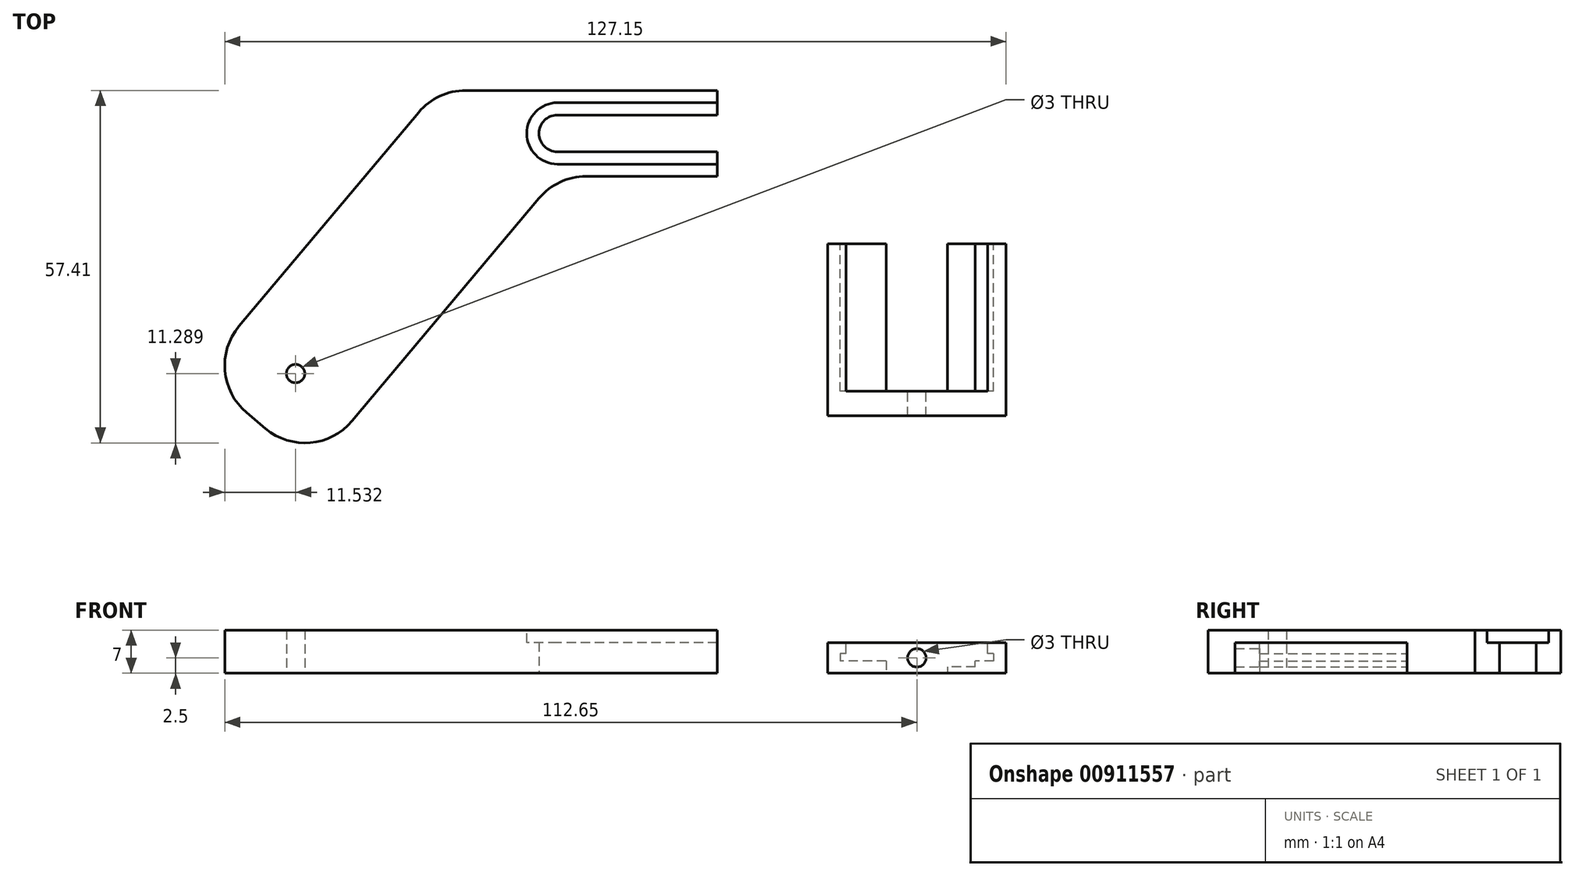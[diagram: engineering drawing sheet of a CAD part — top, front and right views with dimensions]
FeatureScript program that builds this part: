
annotation { "Feature Type Name" : "Feature", "Feature Type Description" : "" }
export const myFeature = defineFeature(function(context is Context, id is Id, definition is map)
    precondition{}
    {
        {
            var Q0;
            Q0=qCreatedBy(makeId("Top.planeOp"),FACE);
            var sketch = newSketch(context, id + "F0", { "sketchPlane" : qUnion([Q0])});
            skLineSegment(sketch, "E0.bottom", {"start": v(0, 7) * mm, "end": v(-40.92, 7) * mm});
            skLineSegment(sketch, "E0.top", {"start": v(0, -7) * mm, "end": v(-21.34, -7) * mm});
            skLineSegment(sketch, "E0.left", {"start": v(0, 7) * mm, "end": v(0, 3) * mm});
            skLineSegment(sketch, "E1.bottom", {"start": v(0, 3) * mm, "end": v(-26, 3) * mm});
            skLineSegment(sketch, "E1.top", {"start": v(0, -3) * mm, "end": v(-26, -3) * mm});
            skArc(sketch, "E2", {"start": v(-26, 3) * mm, "mid": v(-29, 0) * mm, "end": v(-26, -3) * mm});
            skLineSegment(sketch, "E3.trimOffspring", {"start": v(0, -3) * mm, "end": v(0, -7) * mm});
            skLineSegment(sketch, "E4", {"start": v(-29, -10.57) * mm, "end": v(-59.42, -46.83) * mm});
            skLineSegment(sketch, "E5", {"start": v(-73.51, -48.07) * mm, "end": v(-76.58, -45.5) * mm});
            skLineSegment(sketch, "E6", {"start": v(-77.81, -31.4) * mm, "end": v(-48.58, 3.43) * mm});
            skPoint(sketch, "E7.visualSharp", {"position": v(-84.24, -39.07) * mm});
            skArc(sketch, "E7.filletArc", {"start": v(-77.81, -31.4) * mm, "mid": v(-80.11, -38.7) * mm, "end": v(-76.58, -45.5) * mm});
            skPoint(sketch, "E8.visualSharp", {"position": v(-65.85, -54.5) * mm});
            skArc(sketch, "E8.filletArc", {"start": v(-73.51, -48.07) * mm, "mid": v(-66.21, -50.37) * mm, "end": v(-59.42, -46.83) * mm});
            skPoint(sketch, "E9.visualSharp", {"position": v(-45.58, 7) * mm});
            skArc(sketch, "E9.filletArc", {"start": v(-40.92, 7) * mm, "mid": v(-45.15, 6.06) * mm, "end": v(-48.58, 3.43) * mm});
            skPoint(sketch, "E10.visualSharp", {"position": v(-26, -7) * mm});
            skArc(sketch, "E10.filletArc", {"start": v(-21.34, -7) * mm, "mid": v(-25.56, -7.94) * mm, "end": v(-29, -10.57) * mm});
            skCircle(sketch, "E11", {"center": v(-68.62, -39.12) * mm, "radius": 1.5 * mm});
            skPoint(sketch, "E12.start.orphan", {"position": v(-75.05, -46.78) * mm});
            skSolve(sketch);
        }
        {
            var Q0;
            Q0=makeQuery(id+"F0.imprint","IMPRINT",FACE,{"disambiguationData":[TD([[makeQuery(id+"F0.imprint","IMPRINT",EDGE,{"derivedFrom":sQuery(id+"F0.wireOp",EDGE,"E0.bottom")}),1.0]])]});
            extrude(context, id + "F1", {"entities" : qUnion([Q0]), "depth" : 7 * mm, "offsetDistance" : 25 * mm});
        }
        {
            var Q0;
            Q0=makeQuery(id+"F1.opExtrude","CAP_FACE",FACE,{"disambiguationData":[OSD([sQuery(id+"F0.wireOp",EDGE,"E0.bottom"),sQuery(id+"F0.wireOp",EDGE,"E0.top"),sQuery(id+"F0.wireOp",EDGE,"E0.left"),sQuery(id+"F0.wireOp",EDGE,"E1.bottom"),sQuery(id+"F0.wireOp",EDGE,"E1.top"),sQuery(id+"F0.wireOp",EDGE,"E2"),sQuery(id+"F0.wireOp",EDGE,"E3.trimOffspring"),sQuery(id+"F0.wireOp",EDGE,"E4"),sQuery(id+"F0.wireOp",EDGE,"E5"),sQuery(id+"F0.wireOp",EDGE,"E6"),sQuery(id+"F0.wireOp",EDGE,"E7.filletArc"),sQuery(id+"F0.wireOp",EDGE,"E8.filletArc"),sQuery(id+"F0.wireOp",EDGE,"E9.filletArc"),sQuery(id+"F0.wireOp",EDGE,"E10.filletArc")])],"isStart":false});
            var sketch = newSketch(context, id + "F2", { "sketchPlane" : qUnion([Q0])});
            skArc(sketch, "E13", {"start": v(-26, 5) * mm, "mid": v(-31, 0) * mm, "end": v(-26, -5) * mm});
            skLineSegment(sketch, "E14", {"start": v(0, 5) * mm, "end": v(-26, 5) * mm});
            skLineSegment(sketch, "E15", {"start": v(-26, -5) * mm, "end": v(0, -5) * mm});
            skLineSegment(sketch, "E16", {"start": v(0, 5) * mm, "end": v(0, -5) * mm});
            skSolve(sketch);
        }
        {
            var Q0;
            Q0=makeQuery(id+"F2.imprint","IMPRINT",FACE,{"disambiguationData":[TD([[makeQuery(id+"F2.imprint","IMPRINT",EDGE,{"derivedFrom":sQuery(id+"F2.wireOp",EDGE,"E13")}),1.0]])]});
            extrude(context, id + "F3", {"entities" : qUnion([Q0]), "operationType" : NewBodyOperationType.REMOVE, "oppositeDirection" : true, "depth" : 2 * mm, "offsetDistance" : 25 * mm});
        }
        {
            var Q0;
            Q0=qCreatedBy(makeId("Top.planeOp"),FACE);
            var sketch = newSketch(context, id + "F4", { "sketchPlane" : qUnion([Q0])});
            skLineSegment(sketch, "E17.bottom", {"start": v(20, -20) * mm, "end": v(45, -20) * mm});
            skLineSegment(sketch, "E17.top", {"start": v(20, -44) * mm, "end": v(45, -44) * mm});
            skLineSegment(sketch, "E17.left", {"start": v(20, -20) * mm, "end": v(20, -44) * mm});
            skLineSegment(sketch, "E17.right", {"start": v(45, -20) * mm, "end": v(45, -44) * mm});
            skLineSegment(sketch, "E18.bottom", {"start": v(18, -18) * mm, "end": v(47, -18) * mm});
            skLineSegment(sketch, "E18.top", {"start": v(18, -46) * mm, "end": v(47, -46) * mm});
            skLineSegment(sketch, "E18.left", {"start": v(18, -18) * mm, "end": v(18, -46) * mm});
            skLineSegment(sketch, "E18.right", {"start": v(47, -18) * mm, "end": v(47, -46) * mm});
            skSolve(sketch);
        }
        {
            var Q0;
            Q0=makeQuery(id+"F4.imprint","IMPRINT",FACE,{"disambiguationData":[TD([[makeQuery(id+"F4.imprint","IMPRINT",EDGE,{"derivedFrom":sQuery(id+"F4.wireOp",EDGE,"E17.bottom")}),1.0]])]});
            var Q1;
            Q1=makeQuery(id+"F4.imprint","IMPRINT",FACE,{"disambiguationData":[TD([[makeQuery(id+"F4.imprint","IMPRINT",EDGE,{"derivedFrom":sQuery(id+"F4.wireOp",EDGE,"E17.bottom")}),-1.0]])]});
            extrude(context, id + "F5", {"entities" : qUnion([Q0, Q1]), "depth" : 5 * mm, "offsetDistance" : 25 * mm});
        }
        {
            var Q0;
            Q0=makeQuery(id+"F5.opExtrude","SWEPT_FACE",FACE,{"disambiguationData":[OSD([sQuery(id+"F4.wireOp",EDGE,"E18.bottom")])]});
            var sketch = newSketch(context, id + "F6", { "sketchPlane" : qUnion([Q0])});
            skLineSegment(sketch, "E19.bottom", {"start": v(-45, 3.2) * mm, "end": v(-44, 3.2) * mm});
            skLineSegment(sketch, "E19.top", {"start": v(-45, 2) * mm, "end": v(-42, 2) * mm});
            skLineSegment(sketch, "E19.left", {"start": v(-45, 3.2) * mm, "end": v(-45, 2) * mm});
            skLineSegment(sketch, "E19.right", {"start": v(-20, 3.2) * mm, "end": v(-20, 2) * mm});
            skLineSegment(sketch, "E20.top", {"start": v(-37.5, 0) * mm, "end": v(-27.5, 0) * mm});
            skLineSegment(sketch, "E20.left", {"start": v(-37.5, 1) * mm, "end": v(-37.5, 0) * mm});
            skLineSegment(sketch, "E20.right", {"start": v(-27.5, 2) * mm, "end": v(-27.5, 0) * mm});
            skLineSegment(sketch, "E21.top", {"start": v(-44, 5) * mm, "end": v(-21, 5) * mm});
            skLineSegment(sketch, "E21.left", {"start": v(-44, 3.2) * mm, "end": v(-44, 5) * mm});
            skLineSegment(sketch, "E21.right", {"start": v(-21, 3.2) * mm, "end": v(-21, 5) * mm});
            skLineSegment(sketch, "E22.bottom", {"start": v(-42, 1) * mm, "end": v(-37.5, 1) * mm});
            skLineSegment(sketch, "E22.left", {"start": v(-42, 1) * mm, "end": v(-42, 2) * mm});
            skPoint(sketch, "E22.right.start.orphan", {"position": v(-37, 1) * mm});
            skLineSegment(sketch, "E23.trimOffspring", {"start": v(-27.5, 2) * mm, "end": v(-20, 2) * mm});
            skLineSegment(sketch, "E24.trimOffspring", {"start": v(-21, 3.2) * mm, "end": v(-20, 3.2) * mm});
            skSolve(sketch);
        }
        {
            var Q0;
            Q0 = qSketchRegion(id + "F6", true);
            extrude(context, id + "F7", {"entities" : qUnion([Q0]), "operationType" : NewBodyOperationType.REMOVE, "oppositeDirection" : true, "depth" : 24 * mm, "offsetDistance" : 25 * mm});
        }
        {
            var Q0;
            Q0=makeQuery(id+"F7.boolean.opBoolean","COPY",FACE,{"derivedFrom":makeQuery(id+"F7.opExtrude","CAP_FACE",FACE,{"disambiguationData":[OSD([sQuery(id+"F6.wireOp",EDGE,"E19.bottom"),sQuery(id+"F6.wireOp",EDGE,"E19.top"),sQuery(id+"F6.wireOp",EDGE,"E19.left"),sQuery(id+"F6.wireOp",EDGE,"E19.right"),sQuery(id+"F6.wireOp",EDGE,"E20.top"),sQuery(id+"F6.wireOp",EDGE,"E20.left"),sQuery(id+"F6.wireOp",EDGE,"E20.right"),sQuery(id+"F6.wireOp",EDGE,"E21.top"),sQuery(id+"F6.wireOp",EDGE,"E21.left"),sQuery(id+"F6.wireOp",EDGE,"E21.right"),sQuery(id+"F6.wireOp",EDGE,"E22.bottom"),sQuery(id+"F6.wireOp",EDGE,"E22.left"),sQuery(id+"F6.wireOp",EDGE,"E23.trimOffspring"),sQuery(id+"F6.wireOp",EDGE,"E24.trimOffspring")])],"isStart":false})});
            var sketch = newSketch(context, id + "F8", { "sketchPlane" : qUnion([Q0])});
            skCircle(sketch, "E25", {"center": v(-32.5, 2.5) * mm, "radius": 1.5 * mm});
            skPoint(sketch, "E25.centerSnap0", {"position": v(-32.5, 0) * mm});
            skSolve(sketch);
        }
        {
            var Q0;
            Q0 = qSketchRegion(id + "F8", true);
            extrude(context, id + "F9", {"entities" : qUnion([Q0]), "operationType" : NewBodyOperationType.REMOVE, "oppositeDirection" : true, "depth" : 25 * mm, "offsetDistance" : 25 * mm});
        }
    });
